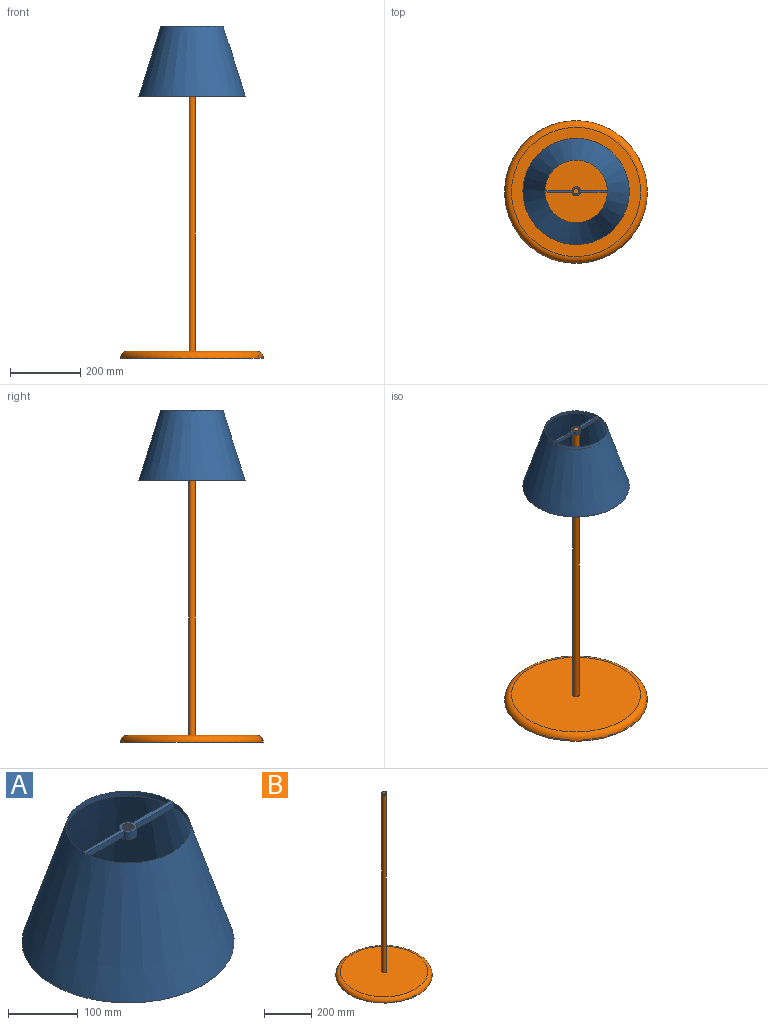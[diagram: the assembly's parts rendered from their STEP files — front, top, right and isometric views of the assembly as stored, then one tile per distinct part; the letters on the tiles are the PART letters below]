
ASSEMBLY  parts=2 mates=1
PART A: 20 faces, bbox 303.3x303.3x201.4 mm
  f0: cylinder r=88.9mm len=177.72mm, axis (0,0,-1), area 2333.2mm2, adj f1,f3,f6,f11
  f1: cone r=152.4mm half-angle=17.4deg, axis (0,0,-1), area 158843.8mm2, adj f0,f2,f4,f9
  f2: cylinder r=88.9mm len=177.69mm, axis (0,0,-1), area 2324.2mm2, adj f1,f3,f7,f12
  f3: cone r=149.98mm half-angle=17.4deg, axis (0,0,-1), area 150419.8mm2, adj f0,f2,f4,f5,f10
  f4: plane 303.21x303.21mm, normal (0,0,-1), area 2512.7mm2, adj f1,f3
  f5: cylinder r=88.9mm len=5.29mm, axis (0,0,1), area 2mm2, adj f3,f6,f7,f8
  f6: plane 76.35x8.89mm, normal (0,1,0), area 678.8mm2, adj f0,f5,f8,f9,f14
  f7: plane 76.55x8.89mm, normal (0,-1,0), area 680.5mm2, adj f2,f5,f8,f9,f14
  f8: plane 76.6x5.29mm, normal (0,0,-1), area 403.7mm2, adj f5,f6,f7,f14
  f9: plane 177.8x25.4mm, normal (0,0,1), area 1160.7mm2, adj f1,f6,f7,f11,f12,f14,f15,f18
  f10: cylinder r=88.9mm len=6.35mm, axis (0,0,1), area 2.4mm2, adj f3,f11,f12,f13
  f11: plane 76.55x8.89mm, normal (0,1,0), area 680.5mm2, adj f0,f9,f10,f13,f14
  f12: plane 76.55x8.89mm, normal (0,-1,0), area 680.5mm2, adj f2,f9,f10,f13,f14
  f13: plane 76.6x6.35mm, normal (0,0,-1), area 484.6mm2, adj f10,f11,f12,f14
  f14: cylinder r=12.7mm len=25.4mm, axis (0,0,1), area 908.9mm2, adj f6,f7,f8,f9,f11,f12,f13,f16
  f15: cylinder r=8.64mm len=17.27mm, axis (0,0,1), area 398.2mm2, adj f9,f16,f17,f18,f19
  f16: plane 25.44x25.44mm, normal (0,0,-1), area 263.6mm2, adj f14,f15,f18,f19
  f17: plane 0.91x0.63mm, normal (0.87,-0.5,0), area 0.3mm2, adj f15,f18,f19
  f18: bspline ~21.62x18.72mm, area 334.7mm2, adj f9,f15,f16,f17,f19
  f19: bspline ~21.62x18.72mm, area 239.5mm2, adj f15,f16,f17,f18
PART B: 15 faces, bbox 441.3x441.3x949.3 mm
  f0: plane 368.3x368.3mm, normal (0,0,1), area 106250.2mm2, adj f2,f4
  f1: plane 406.4x406.4mm, normal (0,0,-1), area 129717.1mm2, adj f2
  f2: torus R=184.15mm, axis (0,0,1), area 36903.3mm2, adj f0,f1
  f3: plane 19.05x19.05mm, normal (0,0,1), area 50.7mm2, adj f4,f5,f9
  f4: cylinder r=9.53mm len=914.4mm, axis (0,0,1), area 54724.4mm2, adj f0,f3
  f5: cylinder r=8.64mm len=17.27mm, axis (0,0,-1), area 157.3mm2, adj f3,f6,f7,f8,f9
  f6: plane 18.08x17.48mm, normal (0,0,1), area 212.3mm2, adj f5,f8,f9
  f7: plane 1.76x0.88mm, normal (0.87,0.5,0), area 0.9mm2, adj f5,f8,f9
  f8: bspline ~19.94x17.27mm, area 579.4mm2, adj f5,f6,f7,f9
  f9: bspline ~22.29x19.3mm, area 311.3mm2, adj f3,f5,f6,f7,f8
  f10: plane 368.3x368.3mm, normal (0,0,-1), area 106382mm2, adj f12,f14
  f11: plane 400.93x400.93mm, normal (0,0,1), area 126246.8mm2, adj f12
  f12: torus R=184.15mm, axis (0,0,1), area 28505.3mm2, adj f10,f11
  f13: plane 13.97x13.97mm, normal (0,0,-1), area 153.3mm2, adj f14
  f14: cylinder r=6.99mm len=914.4mm, axis (0,0,1), area 40131.2mm2, adj f10,f13
PLACE A t=(-106.58,0.2,727.12)mm
PLACE B at identity
MATE fastened A.f14 <-> B.f6  axis (0,0,1) through (-24.08,0.2,891.4)mm
